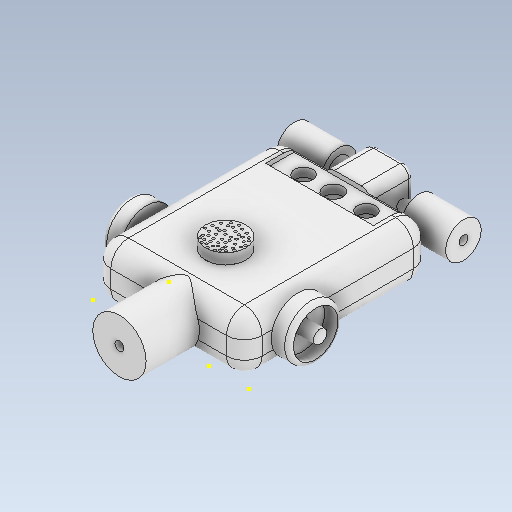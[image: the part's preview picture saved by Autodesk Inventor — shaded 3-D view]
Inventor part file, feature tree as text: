
AUTODESK INVENTOR PART (.ipt)
format: ipt  version: 2021 (Build 250183000, 183)  size: 371,200 bytes
history: native  units: mm
features: sketch x8, other x3
ambient origin geometry x8: Origin, YZ Plane, XZ Plane, XY Plane, X Axis, Y Axis, Z Axis, Center Point
bodies: Solid1 (feature_tree)
feature tree (11):
  other  "robo body part 4.ipt"
  other  "Solid1::robo body part 4.ipt"
  other  "TaggingFeature1"
  sketch  "Sketch5"  dims[d0=30.0mm]
  sketch  "Sketch6"
  sketch  "Sketch22"
  sketch  "Sketch23"
  sketch  "Sketch24"
  sketch  "Sketch28"
  sketch  "Sketch32"
  sketch  "Sketch34"
